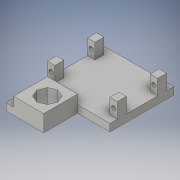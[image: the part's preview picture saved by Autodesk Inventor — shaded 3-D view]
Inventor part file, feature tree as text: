
AUTODESK INVENTOR PART (.ipt)
format: ipt  version: 2016 (Build 200138000, 138)  size: 186,368 bytes
history: native  units: in
note: dims shown in document units (in); Inventor stores cm internally (conversion verified against a paired STEP export)
features: extrude x5, sketch x5
ambient origin geometry x8: Origin, YZ Plane, XZ Plane, XY Plane, X Axis, Y Axis, Z Axis, Center Point
bodies: Solid1 (feature_tree)
feature tree (10):
  extrude  "Extrusion1"  Depth=1.264in
  extrude  "Extrusion2"  Depth=2.3545in
  extrude  "Extrusion3"  Depth=1.9in
  extrude  "Extrusion4"  Depth=0.3in
  extrude  "Extrusion5"  Depth=0.25in
  sketch  "Sketch1"  dims[d0=1.1408in d1=1.264in]
  sketch  "Sketch2"  dims[d6=0.56in d7=0.0in d8=2.3545in]
  sketch  "Sketch3"  dims[d9=0.25in d10=1.9in]
  sketch  "Sketch4"  dims[d11=0.25in d12=0.3in]
  sketch  "Sketch5"  dims[d13=0.25in d14=0.25in d15=0.25in d16=0.3in d17=0.25in d18=0.0in d19=0.25in d20=0.25in d21=0.3in d22=0.25in d23=0.3in d26=0.25in d27=0.512in d28=0.0in d29=2.5505in d30=0.0in d31=0.148in d32=0.148in d33=7.238in d34=0.0in]
